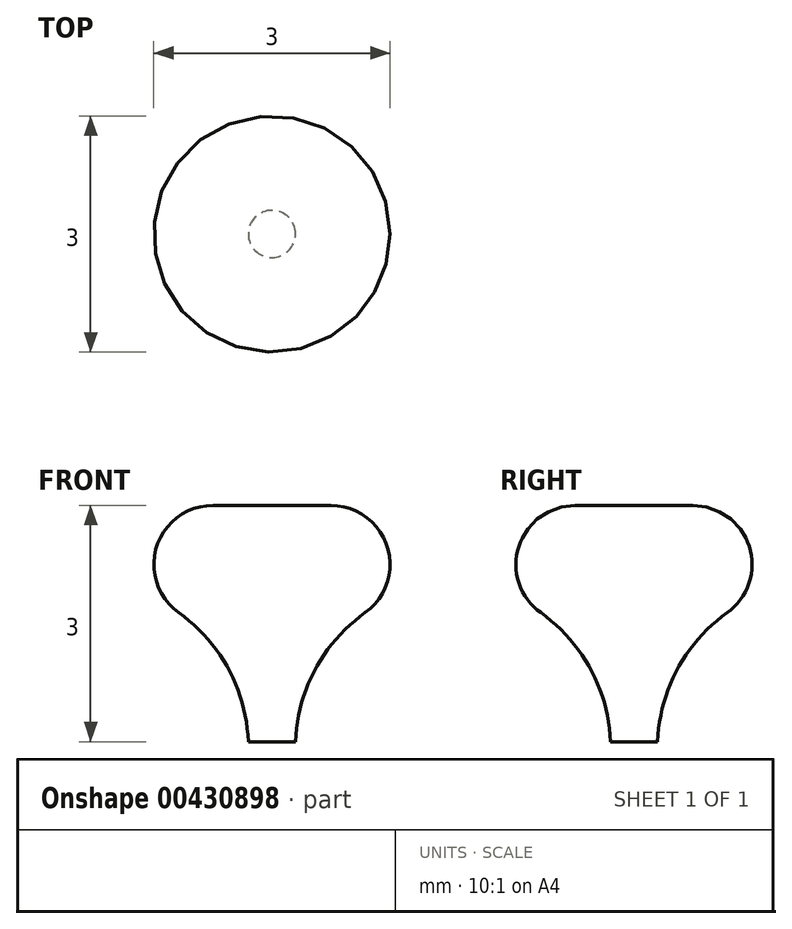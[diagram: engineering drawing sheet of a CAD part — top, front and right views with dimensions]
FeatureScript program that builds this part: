
annotation { "Feature Type Name" : "Feature", "Feature Type Description" : "" }
export const myFeature = defineFeature(function(context is Context, id is Id, definition is map)
    precondition{}
    {
        {
            var Q0;
            Q0=qCreatedBy(makeId("Front.planeOp"),FACE);
            var sketch = newSketch(context, id + "F0", { "sketchPlane" : qUnion([Q0])});
            skLineSegment(sketch, "E0.bottom", {"start": v(0, 3) * mm, "end": v(0.75, 3) * mm});
            skLineSegment(sketch, "E0.left", {"start": v(0, 3) * mm, "end": v(0, 0) * mm});
            skLineSegment(sketch, "E1", {"start": v(0, 40.9) * mm, "end": v(0, 3) * mm, "construction": true});
            skLineSegment(sketch, "E2", {"start": v(0.3, 0) * mm, "end": v(0, 0) * mm});
            skArc(sketch, "E3", {"start": v(1.19, 1.64) * mm, "mid": v(1.46, 2.48) * mm, "end": v(0.75, 3) * mm});
            skArc(sketch, "E4", {"start": v(1.19, 1.64) * mm, "mid": v(0.55, 0.92) * mm, "end": v(0.3, 0) * mm});
            skSolve(sketch);
        }
        {
            var Q0;
            Q0=makeQuery(id+"F0.imprint","IMPRINT",FACE,{"disambiguationData":[TD([[makeQuery(id+"F0.imprint","IMPRINT",EDGE,{"derivedFrom":sQuery(id+"F0.wireOp",EDGE,"E0.bottom")}),-1.0]])]});
            var Q1;
            Q1=sQuery(id+"F0.wireOp",EDGE,"E1");
            revolve(context, id + "F1", {"entities" : qUnion([Q0]), "axis" : qUnion([Q1]), "revolveType" : RevolveType.FULL});
        }
    });
